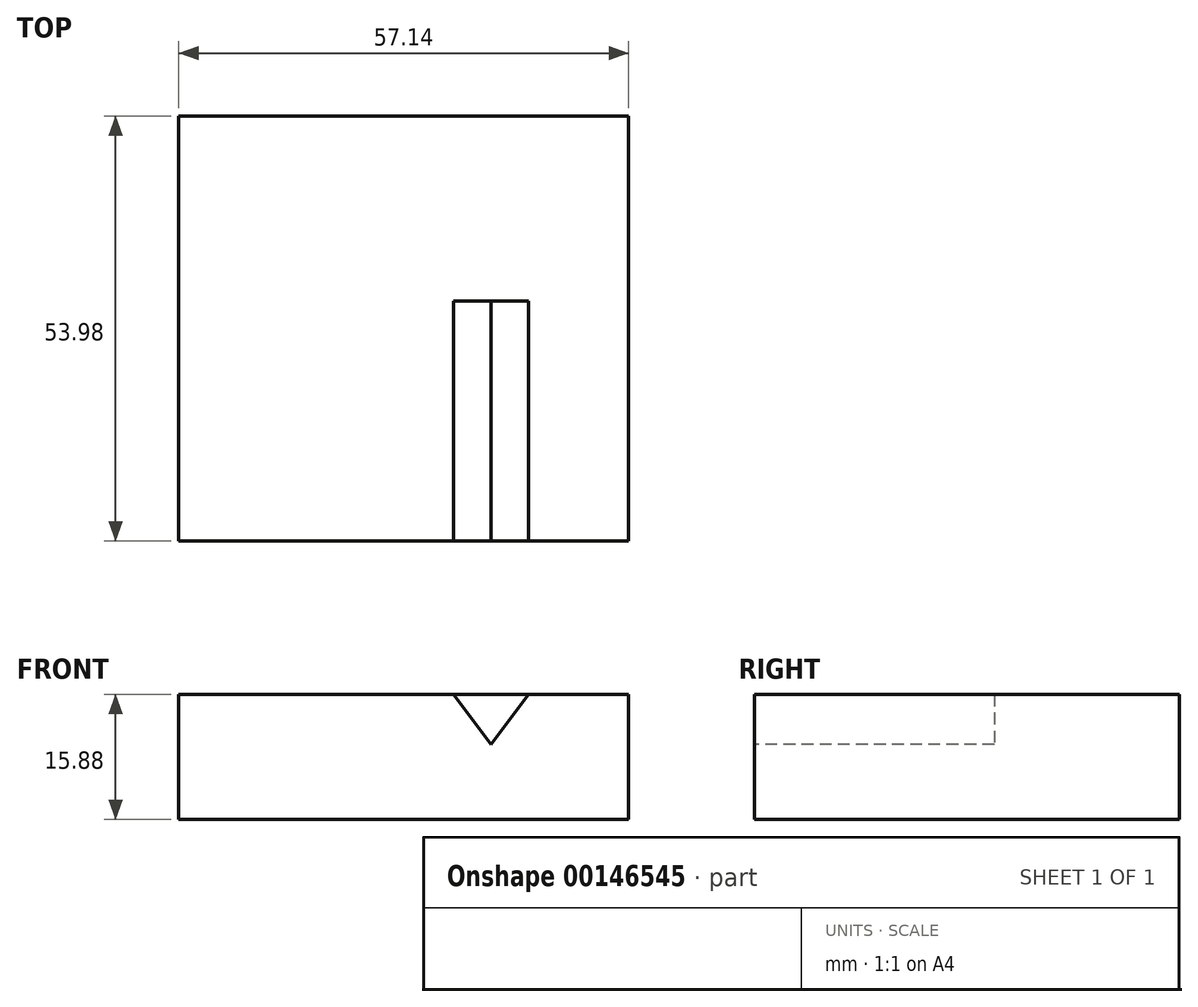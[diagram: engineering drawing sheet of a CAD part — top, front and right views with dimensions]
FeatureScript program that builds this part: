
annotation { "Feature Type Name" : "Feature", "Feature Type Description" : "" }
export const myFeature = defineFeature(function(context is Context, id is Id, definition is map)
    precondition{}
    {
        {
            var Q0;
            Q0=qCreatedBy(makeId("Top.planeOp"),FACE);
            var sketch = newSketch(context, id + "F0", { "sketchPlane" : qUnion([Q0])});
            skLineSegment(sketch, "E0.bottom", {"start": v(28.57, 26.99) * mm, "end": v(-28.58, 26.99) * mm});
            skLineSegment(sketch, "E0.top", {"start": v(28.58, -26.99) * mm, "end": v(-28.57, -26.99) * mm});
            skLineSegment(sketch, "E0.left", {"start": v(28.57, 26.99) * mm, "end": v(28.58, -26.99) * mm});
            skLineSegment(sketch, "E0.right", {"start": v(-28.58, 26.99) * mm, "end": v(-28.57, -26.99) * mm});
            skPoint(sketch, "E0.middle", {"position": v(0, 0) * mm});
            skSolve(sketch);
        }
        {
            var Q0;
            Q0 = qSketchRegion(id + "F0", true);
            extrude(context, id + "F1", {"entities" : qUnion([Q0]), "depth" : 15.88 * mm});
        }
        {
            var Q0;
            Q0=makeQuery(id+"F1.opExtrude","SWEPT_FACE",FACE,{"disambiguationData":[OSD([sQuery(id+"F0.wireOp",EDGE,"E0.top")])]});
            var sketch = newSketch(context, id + "F2", { "sketchPlane" : qUnion([Q0])});
            skLineSegment(sketch, "E1", {"start": v(6.35, 15.88) * mm, "end": v(11.11, 9.53) * mm});
            skLineSegment(sketch, "E2", {"start": v(11.11, 9.52) * mm, "end": v(15.88, 15.88) * mm});
            skLineSegment(sketch, "E3", {"start": v(15.88, 15.88) * mm, "end": v(6.35, 15.88) * mm});
            skSolve(sketch);
        }
        {
            var Q0;
            Q0 = qSketchRegion(id + "F2", true);
            extrude(context, id + "F3", {"entities" : qUnion([Q0]), "operationType" : NewBodyOperationType.REMOVE, "oppositeDirection" : true, "depth" : 30.48 * mm});
        }
    });
